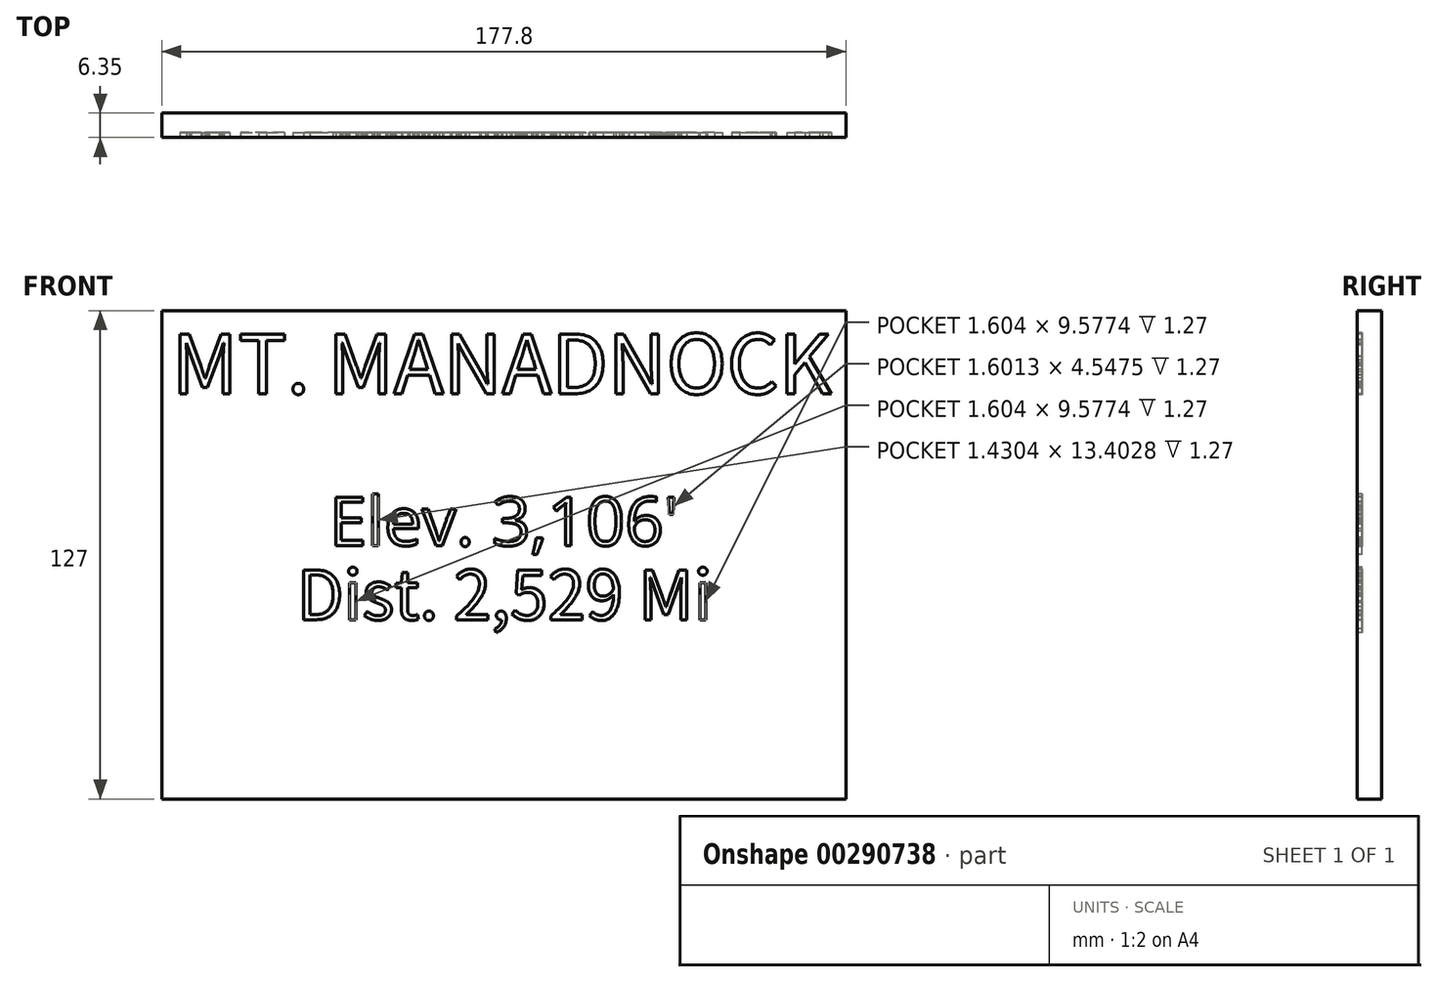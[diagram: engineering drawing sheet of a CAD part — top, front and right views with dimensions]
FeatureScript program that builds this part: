
annotation { "Feature Type Name" : "Feature", "Feature Type Description" : "" }
export const myFeature = defineFeature(function(context is Context, id is Id, definition is map)
    precondition{}
    {
        {
            var Q0;
            Q0=qCreatedBy(makeId("Front.planeOp"),FACE);
            var sketch = newSketch(context, id + "F0", { "sketchPlane" : qUnion([Q0])});
            skLineSegment(sketch, "E0.bottom", {"start": v(177.8, 127) * mm, "end": v(0, 127) * mm});
            skLineSegment(sketch, "E0.top", {"start": v(177.8, 0) * mm, "end": v(0, 0) * mm});
            skLineSegment(sketch, "E0.left", {"start": v(177.8, 127) * mm, "end": v(177.8, 0) * mm});
            skLineSegment(sketch, "E0.right", {"start": v(0, 127) * mm, "end": v(0, 0) * mm});
            skSolve(sketch);
        }
        {
            var Q0;
            Q0 = qSketchRegion(id + "F0", true);
            extrude(context, id + "F1", {"entities" : qUnion([Q0]), "depth" : 6.35 * mm});
        }
        {
            var Q0;
            Q0=makeQuery(id+"F1.opExtrude","CAP_FACE",FACE,{"disambiguationData":[OSD([sQuery(id+"F0.wireOp",EDGE,"E0.bottom"),sQuery(id+"F0.wireOp",EDGE,"E0.top"),sQuery(id+"F0.wireOp",EDGE,"E0.left"),sQuery(id+"F0.wireOp",EDGE,"E0.right")])],"isStart":false});
            var sketch = newSketch(context, id + "F2", { "sketchPlane" : qUnion([Q0])});
            skText(sketch, "E1", { "text": "MT. MANADNOCK", "fontName": "NotoSansCJKjp-Regular.otf"});
            skText(sketch, "E2", { "text": "Elev. 3,106\'", "fontName": "OpenSans-Regular.ttf"});
            skLineSegment(sketch, "E3", {"start": v(88.9, 0) * mm, "end": v(88.9, 127) * mm, "construction": true});
            skText(sketch, "E4", { "text": "Dist. 2,529 Mi", "fontName": "NotoSansCJKjp-Regular.otf"});
            const initialGuessF2  = {"E1": [0.00266, 0.10541, 1, 0, 0.01524], "E2": [0.04348, 0.0659, 1, 0, 0.0127], "E4": [0.0351, 0.04663, 1, 0, 0.0127]};
            skSetInitialGuess(sketch, initialGuessF2);
            skSolve(sketch);
        }
        {
            var Q0;
            Q0 = qSketchRegion(id + "F2", true);
            extrude(context, id + "F3", {"entities" : qUnion([Q0]), "operationType" : NewBodyOperationType.REMOVE, "oppositeDirection" : true, "depth" : 1.27 * mm});
        }
    });
